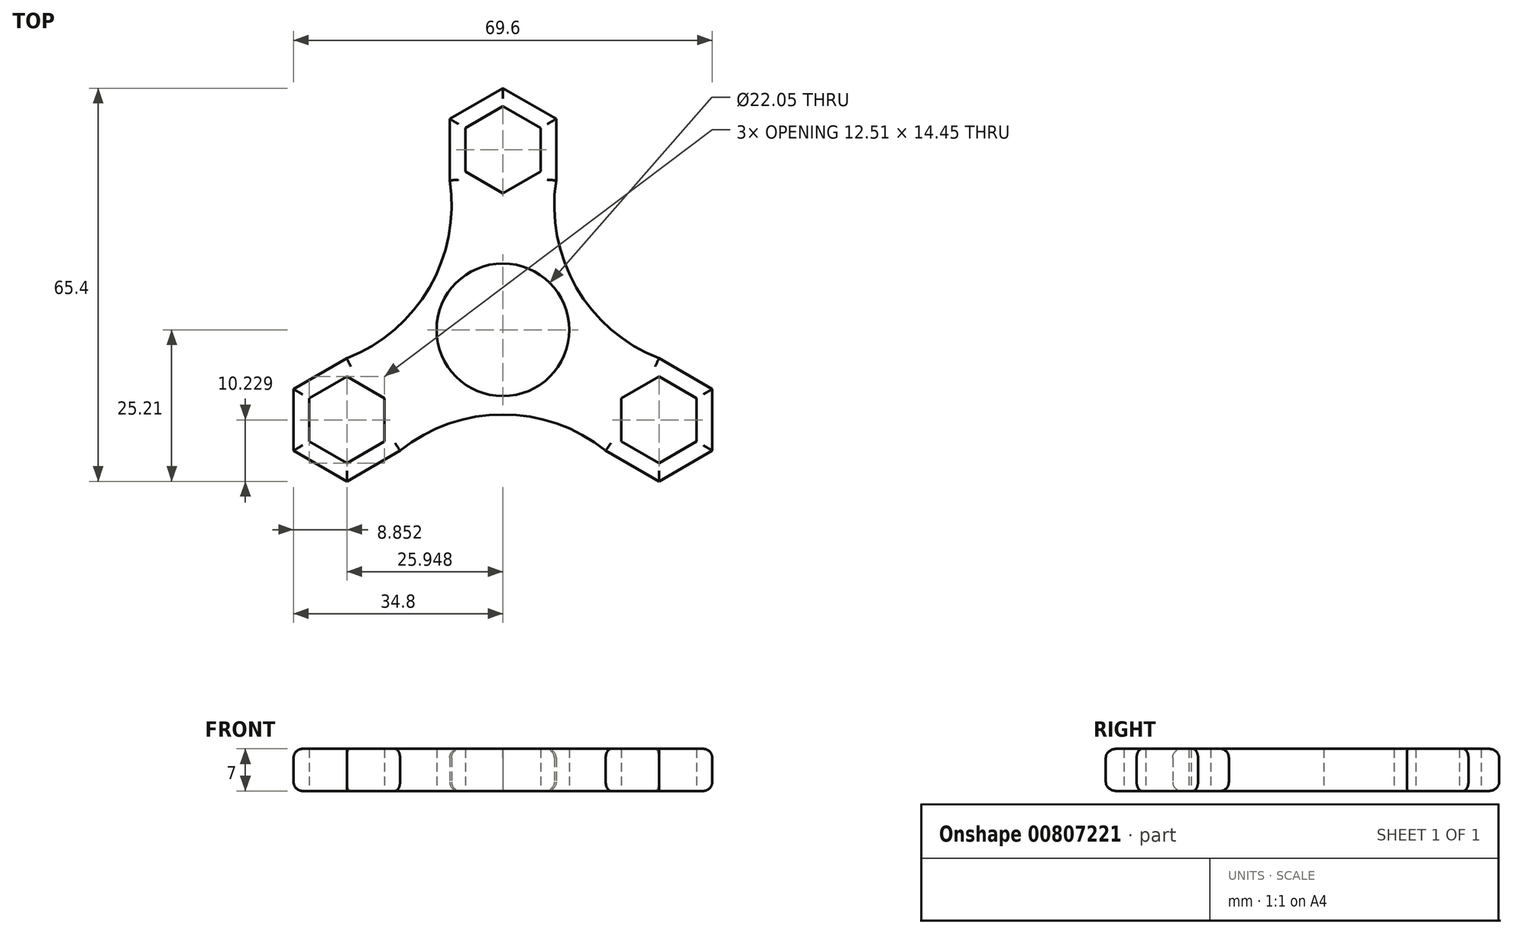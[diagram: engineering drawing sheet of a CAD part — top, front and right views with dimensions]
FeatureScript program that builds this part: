
annotation { "Feature Type Name" : "Feature", "Feature Type Description" : "" }
export const myFeature = defineFeature(function(context is Context, id is Id, definition is map)
    precondition{}
    {
        {
            var Q0;
            Q0=qCreatedBy(makeId("Top.planeOp"),FACE);
            var sketch = newSketch(context, id + "F0", { "sketchPlane" : qUnion([Q0])});
            skCircle(sketch, "E0", {"center": v(0, 0) * mm, "radius": 11.03 * mm});
            skCircle(sketch, "E1.cCircle", {"center": v(0, 29.96) * mm, "radius": 6.26 * mm, "construction": true});
            skLineSegment(sketch, "E1.0", {"start": v(6.26, 33.57) * mm, "end": v(6.26, 26.35) * mm});
            skLineSegment(sketch, "E1.1", {"start": v(6.26, 26.35) * mm, "end": v(0, 22.74) * mm});
            skLineSegment(sketch, "E1.2", {"start": v(0, 22.74) * mm, "end": v(-6.26, 26.35) * mm});
            skLineSegment(sketch, "E1.3", {"start": v(-6.26, 26.35) * mm, "end": v(-6.26, 33.57) * mm});
            skLineSegment(sketch, "E1.4", {"start": v(-6.26, 33.57) * mm, "end": v(0, 37.19) * mm});
            skLineSegment(sketch, "E1.5", {"start": v(0, 37.19) * mm, "end": v(6.26, 33.57) * mm});
            skPoint(sketch, "E1.0.midPoint", {"position": v(6.26, 29.96) * mm});
            skLineSegment(sketch, "E2.0", {"start": v(8.86, 35.07) * mm, "end": v(8.86, 24.85) * mm});
            skLineSegment(sketch, "E2.3", {"start": v(-8.86, 24.85) * mm, "end": v(-8.86, 35.07) * mm});
            skLineSegment(sketch, "E2.4", {"start": v(-8.86, 35.07) * mm, "end": v(0, 40.19) * mm});
            skLineSegment(sketch, "E2.5", {"start": v(0, 40.19) * mm, "end": v(8.86, 35.07) * mm});
            skPoint(sketch, "E2.0.midPoint", {"position": v(8.86, 29.96) * mm});
            skLineSegment(sketch, "E3.1.0", {"start": v(-34.8, -20.1) * mm, "end": v(-34.8, -9.87) * mm});
            skLineSegment(sketch, "E3.1.1", {"start": v(-25.95, -25.2) * mm, "end": v(-34.8, -20.1) * mm});
            skLineSegment(sketch, "E3.1.2", {"start": v(-17.1, -20.1) * mm, "end": v(-25.95, -25.2) * mm});
            skLineSegment(sketch, "E3.1.4", {"start": v(-34.8, -9.87) * mm, "end": v(-25.95, -4.76) * mm});
            skLineSegment(sketch, "E3.1.6", {"start": v(-25.95, -7.76) * mm, "end": v(-19.7, -11.37) * mm});
            skLineSegment(sketch, "E3.1.7", {"start": v(-32.2, -11.37) * mm, "end": v(-25.95, -7.76) * mm});
            skLineSegment(sketch, "E3.1.8", {"start": v(-32.2, -18.6) * mm, "end": v(-32.2, -11.37) * mm});
            skLineSegment(sketch, "E3.1.9", {"start": v(-25.95, -22.2) * mm, "end": v(-32.2, -18.6) * mm});
            skLineSegment(sketch, "E3.1.10", {"start": v(-19.7, -18.6) * mm, "end": v(-25.95, -22.2) * mm});
            skLineSegment(sketch, "E3.1.11", {"start": v(-19.7, -11.37) * mm, "end": v(-19.7, -18.6) * mm});
            skLineSegment(sketch, "E3.2.0", {"start": v(34.8, -20.1) * mm, "end": v(25.95, -25.2) * mm});
            skLineSegment(sketch, "E3.2.1", {"start": v(34.8, -9.87) * mm, "end": v(34.8, -20.1) * mm});
            skLineSegment(sketch, "E3.2.2", {"start": v(25.95, -4.76) * mm, "end": v(34.8, -9.87) * mm});
            skLineSegment(sketch, "E3.2.4", {"start": v(25.95, -25.2) * mm, "end": v(17.1, -20.1) * mm});
            skLineSegment(sketch, "E3.2.6", {"start": v(19.7, -18.6) * mm, "end": v(19.7, -11.37) * mm});
            skLineSegment(sketch, "E3.2.7", {"start": v(25.95, -22.2) * mm, "end": v(19.7, -18.6) * mm});
            skLineSegment(sketch, "E3.2.8", {"start": v(32.2, -18.6) * mm, "end": v(25.95, -22.2) * mm});
            skLineSegment(sketch, "E3.2.9", {"start": v(32.2, -11.37) * mm, "end": v(32.2, -18.6) * mm});
            skLineSegment(sketch, "E3.2.10", {"start": v(25.95, -7.76) * mm, "end": v(32.2, -11.37) * mm});
            skLineSegment(sketch, "E3.2.11", {"start": v(19.7, -11.37) * mm, "end": v(25.95, -7.76) * mm});
            skArc(sketch, "E4", {"start": v(8.86, 24.85) * mm, "mid": v(12.2, 7.05) * mm, "end": v(25.95, -4.76) * mm});
            skArc(sketch, "E5.1.0", {"start": v(-25.95, -4.76) * mm, "mid": v(-12.2, 7.05) * mm, "end": v(-8.86, 24.85) * mm});
            skArc(sketch, "E5.2.0", {"start": v(17.1, -20.1) * mm, "mid": v(0, -14.1) * mm, "end": v(-17.1, -20.1) * mm});
            skSolve(sketch);
        }
        {
            var Q0;
            Q0=makeQuery(id+"F0.imprint","IMPRINT",FACE,{"disambiguationData":[TD([[makeQuery(id+"F0.imprint","IMPRINT",EDGE,{"derivedFrom":sQuery(id+"F0.wireOp",EDGE,"E0")}),-1.0]])]});
            extrude(context, id + "F1", {"entities" : qUnion([Q0]), "depth" : 7 * mm, "offsetDistance" : 25 * mm});
        }
        {
            var Q0;
            Q0=makeQuery(id+"F1.opExtrude","CAP_EDGE",EDGE,{"disambiguationData":[OSD([sQuery(id+"F0.wireOp",EDGE,"E5.2.0")])],"isStart":false});
            var Q1;
            Q1=makeQuery(id+"F1.opExtrude","CAP_EDGE",EDGE,{"disambiguationData":[OSD([sQuery(id+"F0.wireOp",EDGE,"E3.1.2")])],"isStart":false});
            var Q2;
            Q2=makeQuery(id+"F1.opExtrude","CAP_EDGE",EDGE,{"disambiguationData":[OSD([sQuery(id+"F0.wireOp",EDGE,"E3.1.1")])],"isStart":false});
            var Q3;
            Q3=makeQuery(id+"F1.opExtrude","CAP_EDGE",EDGE,{"disambiguationData":[OSD([sQuery(id+"F0.wireOp",EDGE,"E3.1.0")])],"isStart":false});
            var Q4;
            Q4=makeQuery(id+"F1.opExtrude","CAP_EDGE",EDGE,{"disambiguationData":[OSD([sQuery(id+"F0.wireOp",EDGE,"E3.1.4")])],"isStart":false});
            var Q5;
            Q5=makeQuery(id+"F1.opExtrude","CAP_EDGE",EDGE,{"disambiguationData":[OSD([sQuery(id+"F0.wireOp",EDGE,"E5.1.0")])],"isStart":false});
            var Q6;
            Q6=makeQuery(id+"F1.opExtrude","CAP_EDGE",EDGE,{"disambiguationData":[OSD([sQuery(id+"F0.wireOp",EDGE,"E3.2.4")])],"isStart":false});
            var Q7;
            Q7=makeQuery(id+"F1.opExtrude","CAP_EDGE",EDGE,{"disambiguationData":[OSD([sQuery(id+"F0.wireOp",EDGE,"E3.2.0")])],"isStart":false});
            var Q8;
            Q8=makeQuery(id+"F1.opExtrude","CAP_EDGE",EDGE,{"disambiguationData":[OSD([sQuery(id+"F0.wireOp",EDGE,"E3.2.1")])],"isStart":false});
            var Q9;
            Q9=makeQuery(id+"F1.opExtrude","CAP_EDGE",EDGE,{"disambiguationData":[OSD([sQuery(id+"F0.wireOp",EDGE,"E3.2.2")])],"isStart":false});
            var Q10;
            Q10=makeQuery(id+"F1.opExtrude","CAP_EDGE",EDGE,{"disambiguationData":[OSD([sQuery(id+"F0.wireOp",EDGE,"E4")])],"isStart":false});
            var Q11;
            Q11=makeQuery(id+"F1.opExtrude","CAP_EDGE",EDGE,{"disambiguationData":[OSD([sQuery(id+"F0.wireOp",EDGE,"E2.0")])],"isStart":false});
            var Q12;
            Q12=makeQuery(id+"F1.opExtrude","CAP_EDGE",EDGE,{"disambiguationData":[OSD([sQuery(id+"F0.wireOp",EDGE,"E2.5")])],"isStart":false});
            var Q13;
            Q13=makeQuery(id+"F1.opExtrude","CAP_EDGE",EDGE,{"disambiguationData":[OSD([sQuery(id+"F0.wireOp",EDGE,"E2.4")])],"isStart":false});
            var Q14;
            Q14=makeQuery(id+"F1.opExtrude","CAP_EDGE",EDGE,{"disambiguationData":[OSD([sQuery(id+"F0.wireOp",EDGE,"E2.3")])],"isStart":false});
            var Q15;
            Q15=makeQuery(id+"F1.opExtrude","CAP_EDGE",EDGE,{"disambiguationData":[OSD([sQuery(id+"F0.wireOp",EDGE,"E5.2.0")])],"isStart":true});
            var Q16;
            Q16=makeQuery(id+"F1.opExtrude","CAP_EDGE",EDGE,{"disambiguationData":[OSD([sQuery(id+"F0.wireOp",EDGE,"E3.1.2")])],"isStart":true});
            var Q17;
            Q17=makeQuery(id+"F1.opExtrude","CAP_EDGE",EDGE,{"disambiguationData":[OSD([sQuery(id+"F0.wireOp",EDGE,"E3.1.1")])],"isStart":true});
            var Q18;
            Q18=makeQuery(id+"F1.opExtrude","CAP_EDGE",EDGE,{"disambiguationData":[OSD([sQuery(id+"F0.wireOp",EDGE,"E3.1.0")])],"isStart":true});
            var Q19;
            Q19=makeQuery(id+"F1.opExtrude","CAP_EDGE",EDGE,{"disambiguationData":[OSD([sQuery(id+"F0.wireOp",EDGE,"E3.1.4")])],"isStart":true});
            var Q20;
            Q20=makeQuery(id+"F1.opExtrude","CAP_EDGE",EDGE,{"disambiguationData":[OSD([sQuery(id+"F0.wireOp",EDGE,"E5.1.0")])],"isStart":true});
            var Q21;
            Q21=makeQuery(id+"F1.opExtrude","CAP_EDGE",EDGE,{"disambiguationData":[OSD([sQuery(id+"F0.wireOp",EDGE,"E2.3")])],"isStart":true});
            var Q22;
            Q22=makeQuery(id+"F1.opExtrude","CAP_EDGE",EDGE,{"disambiguationData":[OSD([sQuery(id+"F0.wireOp",EDGE,"E2.4")])],"isStart":true});
            var Q23;
            Q23=makeQuery(id+"F1.opExtrude","CAP_EDGE",EDGE,{"disambiguationData":[OSD([sQuery(id+"F0.wireOp",EDGE,"E2.5")])],"isStart":true});
            var Q24;
            Q24=makeQuery(id+"F1.opExtrude","CAP_EDGE",EDGE,{"disambiguationData":[OSD([sQuery(id+"F0.wireOp",EDGE,"E2.0")])],"isStart":true});
            var Q25;
            Q25=makeQuery(id+"F1.opExtrude","CAP_EDGE",EDGE,{"disambiguationData":[OSD([sQuery(id+"F0.wireOp",EDGE,"E4")])],"isStart":true});
            var Q26;
            Q26=makeQuery(id+"F1.opExtrude","CAP_EDGE",EDGE,{"disambiguationData":[OSD([sQuery(id+"F0.wireOp",EDGE,"E3.2.2")])],"isStart":true});
            var Q27;
            Q27=makeQuery(id+"F1.opExtrude","CAP_EDGE",EDGE,{"disambiguationData":[OSD([sQuery(id+"F0.wireOp",EDGE,"E3.2.1")])],"isStart":true});
            var Q28;
            Q28=makeQuery(id+"F1.opExtrude","CAP_EDGE",EDGE,{"disambiguationData":[OSD([sQuery(id+"F0.wireOp",EDGE,"E3.2.0")])],"isStart":true});
            var Q29;
            Q29=makeQuery(id+"F1.opExtrude","CAP_EDGE",EDGE,{"disambiguationData":[OSD([sQuery(id+"F0.wireOp",EDGE,"E3.2.4")])],"isStart":true});
            fillet(context, id + "F2", {"entities" : qUnion([Q0, Q1, Q2, Q3, Q4, Q5, Q6, Q7, Q8, Q9, Q10, Q11, Q12, Q13, Q14, Q15, Q16, Q17, Q18, Q19, Q20, Q21, Q22, Q23, Q24, Q25, Q26, Q27, Q28, Q29]), "radius" : 1.5 * mm, "tangentPropagation" : true, "allowEdgeOverflow" : false});
        }
    });
